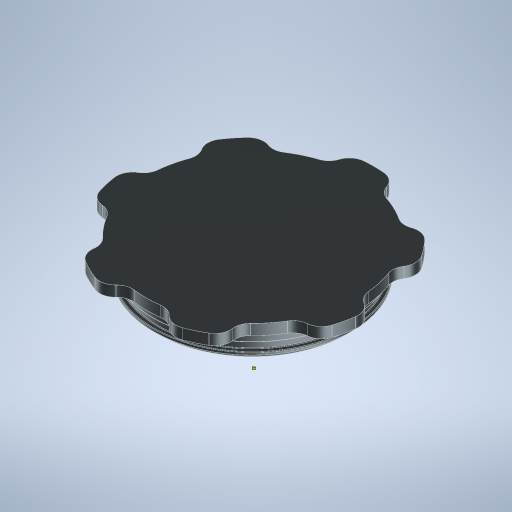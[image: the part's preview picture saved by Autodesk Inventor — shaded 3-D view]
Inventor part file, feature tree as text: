
AUTODESK INVENTOR PART (.ipt)
format: ipt  version: 2024.3 (Build 283343000, 343)  size: 371,712 bytes
history: native  units: mm
features: fillet x2, sketch x2, other x1, revolve x1, extrude x1, pattern_circular x1, chamfer x1
ambient origin geometry x8: Origin, YZ Plane, XZ Plane, XY Plane, X Axis, Y Axis, Z Axis, Center Point
bodies: Body1 (feature_tree)
feature tree (9):
  other  "Sólido1"
  revolve  "Revolución1"  [1 undecoded]
  extrude  "Extrusión2"  Depth=0.25mm
  fillet  "Empalme5"  Radius=0.275mm
  pattern_circular  "Patrón circular3"  [2 undecoded]
  fillet  "Empalme6"  Radius=3.7mm
  chamfer  "Chaflán1"  Angle=90.0deg  [1 undecoded]
  sketch  "Boceto1"  dims[d1=5.0mm d4=0.0mm]
  sketch  "Boceto6"  dims[d6=0.872665mm d7=94.0mm d9=0.275mm d10=2.1mm d11=3.7mm d12=90.0deg d14=89.8mm d88=20.0mm d89=4.363323mm d90=7.5mm d91=10.0mm d92=0.0mm d93=7.5mm d94=70.0mm d95=360.0deg d98=0.25mm d99=2.0mm d100=2.0mm d101=45.0deg]
note: 4 required parameter values undecoded (feature->parameter linkage not recoverable at this tier; creation-order binding heuristic only, values carry confidence <= 0.55)